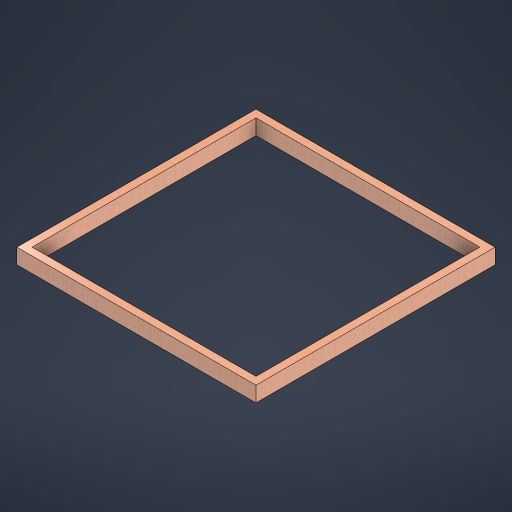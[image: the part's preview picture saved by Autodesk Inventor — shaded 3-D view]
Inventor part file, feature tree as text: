
AUTODESK INVENTOR PART (.ipt)
format: ipt  version: 2023.1 (Build 271208000, 208)  size: 242,176 bytes
history: native  units: in
note: dims shown in document units (in); Inventor stores cm internally (conversion verified against a paired STEP export)
features: extrude x1, sketch x1
ambient origin geometry x8: Origin, YZ Plane, XZ Plane, XY Plane, X Axis, Y Axis, Z Axis, Center Point
bodies: Solid1 (feature_tree)
feature tree (2):
  extrude  "Extrusion1"  Depth=1.0in
  sketch  "Sketch1"  dims[d0=29.25in d2=1.0in d3=1.0in d4=2.0in d5=0.0in]
